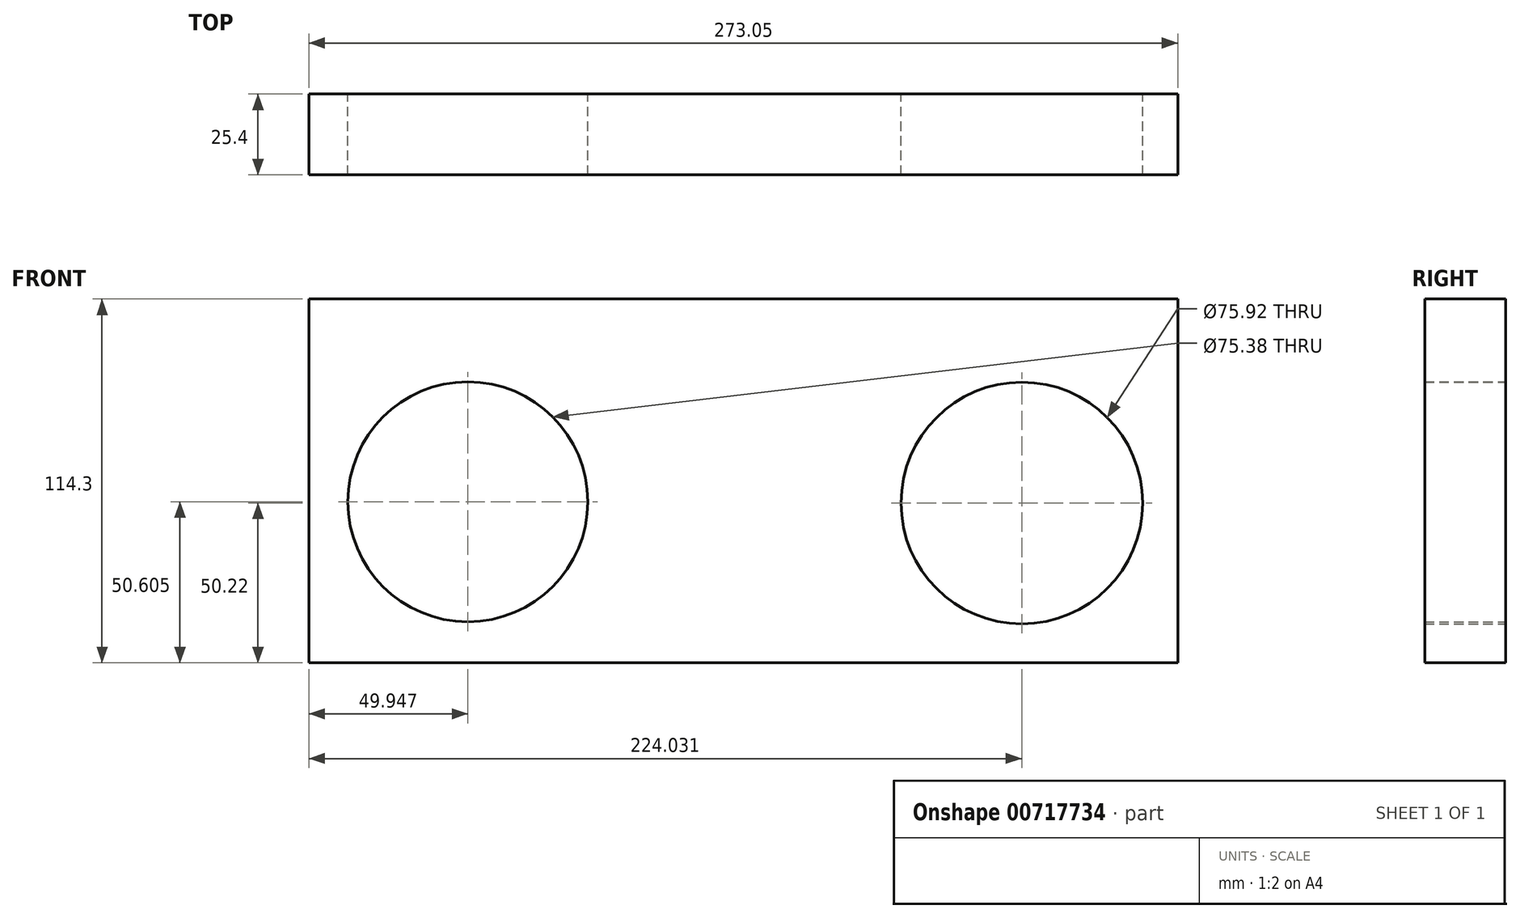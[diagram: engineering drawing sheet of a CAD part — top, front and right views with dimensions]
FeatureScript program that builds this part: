
annotation { "Feature Type Name" : "Feature", "Feature Type Description" : "" }
export const myFeature = defineFeature(function(context is Context, id is Id, definition is map)
    precondition{}
    {
        {
            var Q0;
            Q0=qCreatedBy(makeId("Front.planeOp"),FACE);
            var sketch = newSketch(context, id + "F0", { "sketchPlane" : qUnion([Q0])});
            skLineSegment(sketch, "E0.bottom", {"start": v(0, 0) * mm, "end": v(273.05, 0) * mm});
            skLineSegment(sketch, "E0.top", {"start": v(0, 114.3) * mm, "end": v(273.05, 114.3) * mm});
            skLineSegment(sketch, "E0.left", {"start": v(0, 0) * mm, "end": v(0, 114.3) * mm});
            skLineSegment(sketch, "E0.right", {"start": v(273.05, 0) * mm, "end": v(273.05, 114.3) * mm});
            skSolve(sketch);
        }
        {
            var Q0;
            Q0=makeQuery(id+"F0.imprint","IMPRINT",FACE,{"disambiguationData":[TD([[makeQuery(id+"F0.imprint","IMPRINT",EDGE,{"derivedFrom":sQuery(id+"F0.wireOp",EDGE,"E0.bottom")}),1.0]])]});
            var sketch = newSketch(context, id + "F1", { "sketchPlane" : qUnion([Q0])});
            skCircle(sketch, "E1", {"center": v(49.95, 50.6) * mm, "radius": 37.7 * mm});
            skCircle(sketch, "E2", {"center": v(224.03, 50.22) * mm, "radius": 37.96 * mm});
            skSolve(sketch);
        }
        {
            var Q0;
            Q0=makeQuery(id+"F0.imprint","IMPRINT",FACE,{"disambiguationData":[TD([[makeQuery(id+"F0.imprint","IMPRINT",EDGE,{"derivedFrom":sQuery(id+"F0.wireOp",EDGE,"E0.bottom")}),1.0]])]});
            extrude(context, id + "F2", {"entities" : qUnion([Q0]), "depth" : 25.4 * mm, "offsetDistance" : 25.4 * mm});
        }
        {
            var Q0;
            Q0=makeQuery(id+"F2.opExtrude","CAP_FACE",FACE,{"disambiguationData":[OSD([sQuery(id+"F0.wireOp",EDGE,"E0.bottom"),sQuery(id+"F0.wireOp",EDGE,"E0.top"),sQuery(id+"F0.wireOp",EDGE,"E0.left"),sQuery(id+"F0.wireOp",EDGE,"E0.right")])],"isStart":false});
            var sketch = newSketch(context, id + "F3", { "sketchPlane" : qUnion([Q0])});
            skSolve(sketch);
        }
        {
            var Q0;
            Q0 = qSketchRegion(id + "F1", true);
            extrude(context, id + "F4", {"entities" : qUnion([Q0]), "operationType" : NewBodyOperationType.REMOVE, "oppositeDirection" : true, "depth" : 25.4 * mm, "offsetDistance" : 25.4 * mm});
        }
        {
            var Q0;
            Q0 = qSketchRegion(id + "F1", true);
            extrude(context, id + "F5", {"entities" : qUnion([Q0]), "operationType" : NewBodyOperationType.REMOVE, "oppositeDirection" : true, "depth" : 25.4 * mm, "offsetDistance" : 25.4 * mm});
        }
        {
            var Q0;
            Q0 = qSketchRegion(id + "F1", true);
            extrude(context, id + "F6", {"entities" : qUnion([Q0]), "operationType" : NewBodyOperationType.REMOVE, "oppositeDirection" : true, "depth" : 25.4 * mm, "offsetDistance" : 25.4 * mm});
        }
        {
            var Q0;
            Q0 = qSketchRegion(id + "F1", true);
            extrude(context, id + "F7", {"entities" : qUnion([Q0]), "operationType" : NewBodyOperationType.REMOVE, "depth" : 25.4 * mm, "offsetDistance" : 25.4 * mm});
        }
    });
